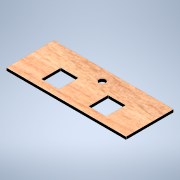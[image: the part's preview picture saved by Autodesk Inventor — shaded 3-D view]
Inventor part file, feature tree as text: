
AUTODESK INVENTOR PART (.ipt)
format: ipt  version: 2021 (Build 250183000, 183)  size: 131,072 bytes
history: native  units: mm
features: extrude x1, sketch x1
ambient origin geometry x8: Origin, YZ Plane, XZ Plane, XY Plane, X Axis, Y Axis, Z Axis, Center Point
bodies: Volumenkörper1 (feature_tree)
feature tree (2):
  extrude  "Extrusion1"  Depth=3.0mm TaperAngle=0.0deg
  sketch  "Skizze1"  dims[d0=129.5mm d2=3.0mm d3=0.0mm d4=19.0mm d5=21.0mm d7=8.2mm d8=51.5mm d9=32.2mm d10=7.0mm d11=9.0mm]
